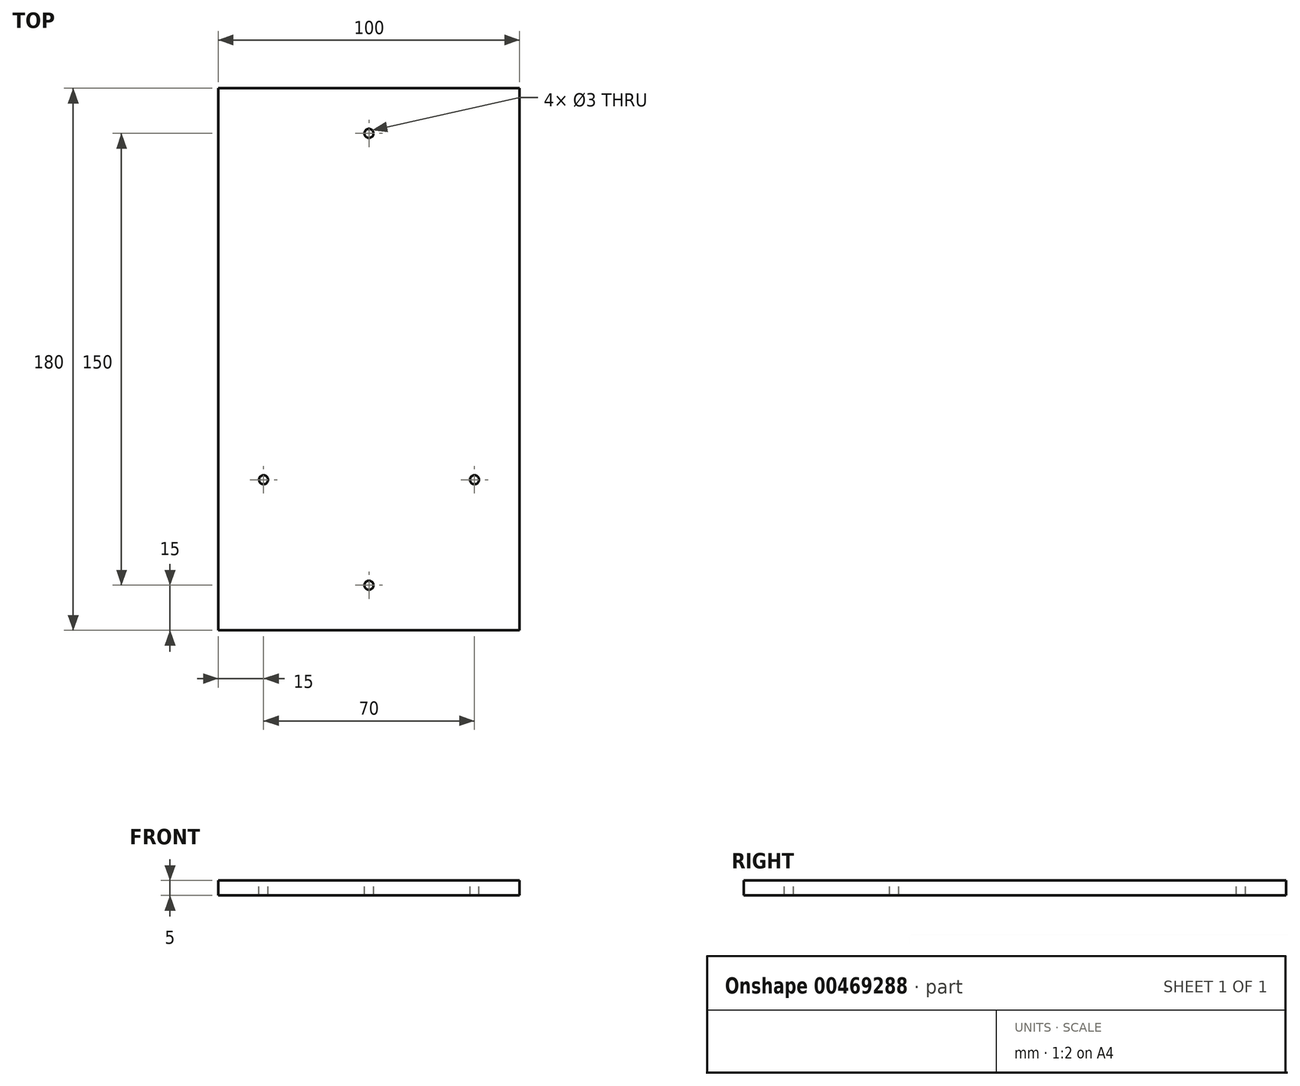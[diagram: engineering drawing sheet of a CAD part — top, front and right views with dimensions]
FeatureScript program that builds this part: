
annotation { "Feature Type Name" : "Feature", "Feature Type Description" : "" }
export const myFeature = defineFeature(function(context is Context, id is Id, definition is map)
    precondition{}
    {
        {
            var Q0;
            Q0=qCreatedBy(makeId("Top.planeOp"),FACE);
            var sketch = newSketch(context, id + "F0", { "sketchPlane" : qUnion([Q0])});
            skLineSegment(sketch, "E0.bottom", {"start": v(-50, 90) * mm, "end": v(50, 90) * mm});
            skLineSegment(sketch, "E0.top", {"start": v(-50, -90) * mm, "end": v(50, -90) * mm});
            skLineSegment(sketch, "E0.left", {"start": v(-50, 90) * mm, "end": v(-50, -90) * mm});
            skLineSegment(sketch, "E0.right", {"start": v(50, 90) * mm, "end": v(50, -90) * mm});
            skPoint(sketch, "E0.middle", {"position": v(0, 0) * mm});
            skSolve(sketch);
        }
        {
            var Q0;
            Q0=makeQuery(id+"F0.imprint","IMPRINT",FACE,{"disambiguationData":[TD([[makeQuery(id+"F0.imprint","IMPRINT",EDGE,{"derivedFrom":sQuery(id+"F0.wireOp",EDGE,"E0.bottom")}),-1.0]])]});
            extrude(context, id + "F1", {"entities" : qUnion([Q0]), "oppositeDirection" : true, "depth" : 5 * mm, "offsetDistance" : 25 * mm});
        }
        {
            var Q0;
            Q0=makeQuery(id+"F1.opExtrude","CAP_FACE",FACE,{"disambiguationData":[OSD([sQuery(id+"F0.wireOp",EDGE,"E0.bottom"),sQuery(id+"F0.wireOp",EDGE,"E0.top"),sQuery(id+"F0.wireOp",EDGE,"E0.left"),sQuery(id+"F0.wireOp",EDGE,"E0.right")])],"isStart":true});
            var sketch = newSketch(context, id + "F2", { "sketchPlane" : qUnion([Q0])});
            skPoint(sketch, "E1", {"position": v(-35, 75) * mm});
            skPoint(sketch, "E2", {"position": v(35, 75) * mm});
            skPoint(sketch, "E3", {"position": v(-35, -75) * mm});
            skPoint(sketch, "E4", {"position": v(35, -75) * mm});
            skPoint(sketch, "E5", {"position": v(-35, -40) * mm});
            skPoint(sketch, "E6", {"position": v(35, -40) * mm});
            skPoint(sketch, "E7", {"position": v(0, -75) * mm});
            skPoint(sketch, "E8", {"position": v(0, 75) * mm});
            skSolve(sketch);
        }
        {
            var Q0;
            Q0=sQuery(id+"F2.wireOp",VERTEX,"E5");
            var Q1;
            Q1=sQuery(id+"F2.wireOp",VERTEX,"E7");
            var Q2;
            Q2=sQuery(id+"F2.wireOp",VERTEX,"E6");
            var Q3;
            Q3=sQuery(id+"F2.wireOp",VERTEX,"E8");
            var Q4;
            Q4=makeQuery(id+"F1.opExtrude","SWEPT_BODY",BODY,{"disambiguationData":[OSD([sQuery(id+"F0.wireOp",EDGE,"E0.bottom"),sQuery(id+"F0.wireOp",EDGE,"E0.top"),sQuery(id+"F0.wireOp",EDGE,"E0.left"),sQuery(id+"F0.wireOp",EDGE,"E0.right")])]});
            hole(context, id + "F3", {"style" : HoleStyle.SIMPLE, "endStyle" : HoleEndStyle.THROUGH, "holeDiameter" : 3 * mm, "isTappedThrough" : true, "tappedDepth" : 12 * mm, "tapClearance" : 3, "locations" : qUnion([Q0, Q1, Q2, Q3]), "scope" : qUnion([Q4])});
        }
    });
